# Revit family: Gira_128900
name_source: partatom
category: Elektroinstallationen
revit_build: Autodesk Revit 2017 (Build: 20160225_1515(x64)
units: mm (PartAtom-declared; Revit-internal decimal feet)

## family parameters
Basisbauteil = Fläche
Beim Laden mit Abzugskörper schneiden = Nein
Bemaßung runder Anschluss = Durchmesser verwenden
Beschriftungsausrichtung beibehalten = Nein
Gemeinsam genutzt = Nein
Raumberechnungspunkt = Nein
Teiletyp = Normal

## types (1)
- Gira_128900
    BIM = https://media.stage.bim.site 2f.rfa
    Beschreibung = Türkommunikations-Schaltaktor  REG Merkmale: - Schaltaktor zum Schalten von Licht, Ansteuern eines Türöffners an Nebentüren oder anderen Funktionen über den Gira Türkommunikations-Bus. - Ansteuerung eines potenzialfreien Schaltkontakts 230 V   10 A über den 2-Draht-Bus. - Der Schaltaktor ist ansteuerbar über:   die Tasten Tür" und "Licht" an der Wohnungsstation,   die Ruftaste an der Türstation,   die Ruftaste an der Wohnungsstation,   die Tasten eines Telefons (in Verbindung mit TKS-TK-Gateway). - Der Schaltaktor lässt sich in fünf verschiedenen Betriebsarten betreiben: Schalten, Timer s, Timer min, Impuls und Türöffner. - Impulsfunktion zur Ansteuerung vorhandener Treppenhausautomaten. - Binäreingang zum Schalten von Funktionen über einen angeschlossenen mechanischen Taster. - Schaltzeit abhängig von der eingestellten Funktion stufenlos einstellbar von 1 bis 10 s bzw. 1 bis 10 min.  Hinweise : - Der Schaltaktor ist für den Einbau in die Unterverteilung vorgesehen. Ist dies nicht möglich, handelsüblichen Aufputzverteiler verwenden. - Mit dieser Komponente ist der Aufbau von Türkommunikationsanlagen mit mehr als 30 Teilnehmern möglich."
    Datenblatt = https://katalog.gira.de
    Funktion = schalten
    GTIN = 4010337289005
    HAN = 128900
    Hersteller = Gira
    Installationstechnik = Bus-System
    Produktseite = http://katalog.gira.de
    Typname = TKS-Schaltaktor REG Türko
    URL = https://www.gira.de
    Vorgabe-Ansicht = 1219 mm

## geometry (parser evidence)
native form markers: Sweep x2
no freeform markers — native parametric forms only
